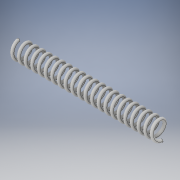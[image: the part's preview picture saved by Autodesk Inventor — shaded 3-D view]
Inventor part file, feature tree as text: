
AUTODESK INVENTOR PART (.ipt)
format: ipt  version: 2018.3 (Build 223284000, 284)  size: 363,008 bytes
history: native  units: in
note: dims shown in document units (in); Inventor stores cm internally (conversion verified against a paired STEP export)
features: helix x1, sketch x1
ambient origin geometry x8: Origin, YZ Plane, XZ Plane, XY Plane, X Axis, Y Axis, Z Axis, Center Point
bodies: Solid1 (feature_tree)
feature tree (2):
  helix  "Coil1"  [1 undecoded]
  sketch  "Sketch1"  dims[d1=0.273in d2=0.045in d3=1.0in d4=2.156in d5=8.4646in d6=0.0011in d7=90.0deg d8=90.0deg d9=0.0in d10=0.0in]
note: 1 required parameter value undecoded (feature->parameter linkage not recoverable at this tier; creation-order binding heuristic only, values carry confidence <= 0.55)
